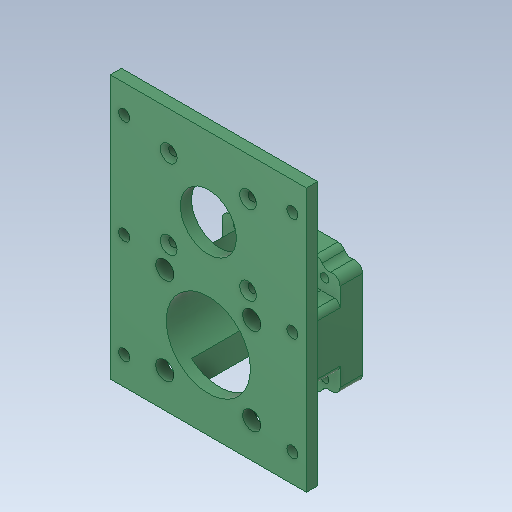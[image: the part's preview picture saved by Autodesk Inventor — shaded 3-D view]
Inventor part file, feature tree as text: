
AUTODESK INVENTOR PART (.ipt)
format: ipt  version: 2020 (Build 240168000, 168)  size: 437,248 bytes
history: native  units: mm
features: sketch x12, extrude x11, other x5, fillet x4, projected_geometry x4, pattern_circular x3, direct_edit x3, chamfer x2, hole x1, mirror x1, reference x1
ambient origin geometry x8: Origin, YZ Plane, XZ Plane, XY Plane, X Axis, Y Axis, Z Axis, Center Point
bodies: Solid1 (feature_tree)
feature tree (47):
  extrude  "Extrusion1"  Depth=30.0mm TaperAngle=0.0deg
  extrude  "Extrusion2"  Depth=10.0mm
  pattern_circular  "Circular Pattern2"  Count=2 Angle=360.0deg
  extrude  "Extrusion3"  Depth=4.0mm
  fillet  "Fillet2"  Radius=4.0mm
  pattern_circular  "Circular Pattern3"  [2 undecoded]
  extrude  "Extrusion4"  Depth=4.0mm TaperAngle=45.0deg
  fillet  "Fillet4"  [1 undecoded]
  fillet  "Fillet5"  Radius=3.25mm
  extrude  "Extrusion10"  Depth=2.0mm TaperAngle=0.0deg
  direct_edit  "Direct Edit3"
  direct_edit  "Direct Edit4"
  chamfer  "Chamfer3"  Distance=28.0mm
  direct_edit  "Direct Edit5"
  fillet  "Fillet6"  Radius=25.0mm
  extrude  "Extrusion13"  TaperAngle=0.0deg  [1 undecoded]
  extrude  "Extrusion14"  Depth=20.0mm
  extrude  "Extrusion16"  Depth=2.0mm TaperAngle=0.0deg
  hole  "Hole1"  [1 undecoded]
  extrude  "Extrusion17"  Depth=4.0mm
  mirror  "Mirror3"
  extrude  "Extrusion18"  Depth=2.0mm
  chamfer  "Chamfer4"  Distance=7.0mm
  pattern_circular  "Circular Pattern4"  [2 undecoded]
  extrude  "Extrusion19"  Depth=10.0mm
  sketch  "Sketch1"  dims[d0=34.0mm d1=0.0mm d2=30.0mm d3=0.0mm]
  reference  "Reference1"
  sketch  "Sketch2"  dims[d8=40.0mm d9=360.0deg d11=10.0mm]
  sketch  "Sketch3"  dims[d12=60.25mm d13=0.0mm]
  sketch  "Sketch4"  dims[d14=2.0mm d15=20.0mm d16=360.0deg]
  sketch  "Sketch11"  dims[d18=50.0mm d19=50.0mm d20=4.0mm d21=0.0mm]
  sketch  "Sketch14"  dims[d37=2.75mm]
  projected_geometry  "Projected Loop1"
  sketch  "Sketch15"  dims[d38=2.75mm]
  sketch  "Sketch17"  dims[d41=8.5mm d42=0.0mm]
  projected_geometry  "Projected Loop2"
  sketch  "Sketch18"  dims[d62=25.0mm]
  sketch  "Sketch20"  dims[d72=10.0mm]
  projected_geometry  "Projected Loop3"
  sketch  "Sketch21"  dims[d73=10.0mm]
  sketch  "Sketch22"  dims[d74=6.5mm d75=4.0mm d76=4.0mm d77=2.0mm d78=45.0deg d79=-2.5mm d80=3.25mm d81=41.0mm d82=0.0mm d83=28.0mm d84=25.0mm d85=0.0mm d86=20.0mm d87=44.0mm d88=0.0mm d94=10.0mm d95=0.0mm d96=4.0mm d97=5.0mm d98=7.0mm d99=4.0mm d100=10.0mm d101=5.0mm d102=4.0mm d103=6.0mm d104=6.0mm d105=2.0mm d106=90.0deg d107=8.0mm d108=120.0deg d112=4.0mm d113=5.0mm d114=37.0mm d118=10.0mm d119=0.0mm d120=20.0mm d121=135.0deg d122=3.0mm d123=7.5mm d124=0.0mm d125=40.0mm d126=360.0deg d128=1.5mm d129=2.0mm d130=45.0deg d131=3.0mm d132=0.0mm]
  projected_geometry  "Projected Loop4"
  other  "КВ33.000.100 - Блок переключение передач.iam"
  other  "nema 17 motor:1"
  other  "Size1"
  other  "Size2"
  other  "Size3"
note: 7 required parameter values undecoded (feature->parameter linkage not recoverable at this tier; creation-order binding heuristic only, values carry confidence <= 0.55)
